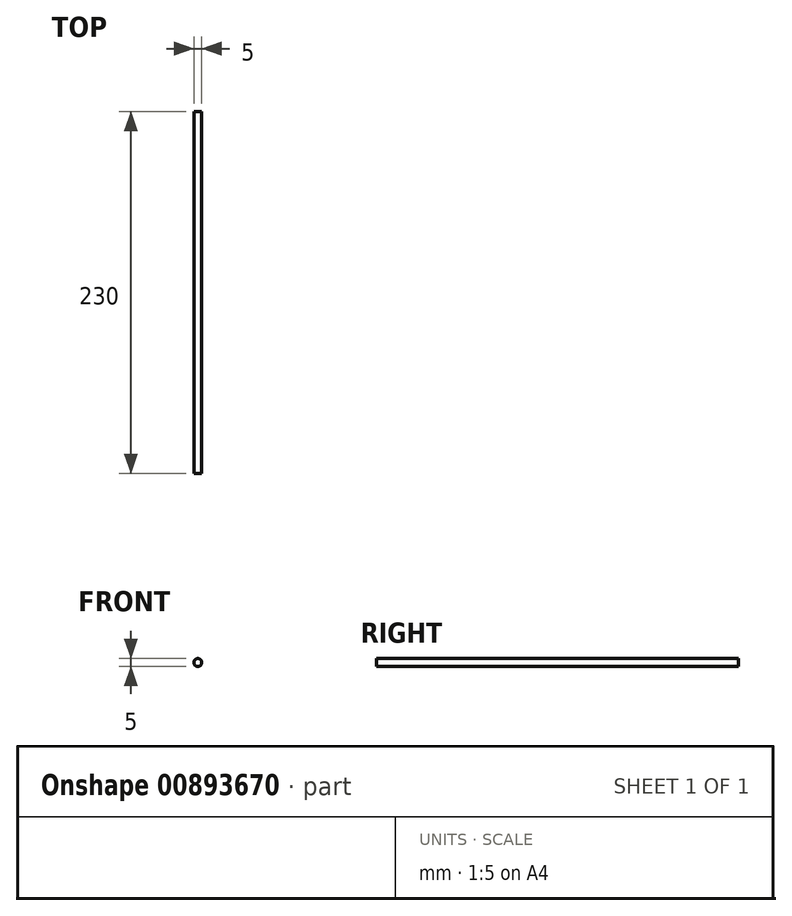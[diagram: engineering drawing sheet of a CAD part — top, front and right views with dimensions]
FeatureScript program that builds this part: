
annotation { "Feature Type Name" : "Feature", "Feature Type Description" : "" }
export const myFeature = defineFeature(function(context is Context, id is Id, definition is map)
    precondition{}
    {
        {
            var Q0;
            Q0=qCreatedBy(makeId("Front.planeOp"),FACE);
            var sketch = newSketch(context, id + "F0", { "sketchPlane" : qUnion([Q0])});
            skCircle(sketch, "E0", {"center": v(0, 0) * mm, "radius": 2.5 * mm});
            skSolve(sketch);
        }
        {
            var Q0;
            Q0=makeQuery(id+"F0.imprint","IMPRINT",FACE,{"disambiguationData":[TD([[makeQuery(id+"F0.imprint","IMPRINT",EDGE,{"derivedFrom":sQuery(id+"F0.wireOp",EDGE,"E0")}),1.0]])]});
            extrude(context, id + "F1", {"entities" : qUnion([Q0]), "endBound" : BoundingType.SYMMETRIC, "depth" : 230 * mm, "offsetDistance" : 25 * mm});
        }
    });
